# Revit family: Accessory-Towel_Arm-KOHLER-AVID-K-97498T
name_source: partatom
category: Specialty Equipment
revit_build: Autodesk Revit 2017 (Build: 20160225_1515(x64)
units: mm (PartAtom-declared; Revit-internal decimal feet)

## family parameters
Cut with Voids When Loaded = No
Host = Face
OmniClass Number = 23.31.25.25
OmniClass Title = Towel Bars
Part Type = Normal
Room Calculation Point = No
Round Connector Dimension = Use Diameter
Shared = No

## types (10) — shared parameters
ADA Compliant = No
Assembly Code = C1030200
Date Modified = 06/09/2020
Default Elevation = 42"
Description = Towel Arm
Height = 1 3/4"
Length = 2 3/4"
Manufacturer = KOHLER Co.
Master Format 2014 = 10 28 00
Master Format 2014 Name = Toilet, Bath, and Laundry Accessories
Material = Premium Metal Construction
Product Documentation Link = http://files.kohler.com.cn
Product Name = AVID
Product Page URL = http://www.kohler.com.cn
URL = http://www.kohler.com.cn
WaterSense Certified = No
Width = 9 15/16"

## per-type parameters (varying)
| type | Finish | Model | Type |
| CP-Polished Chrome | Kohler-Metal-CP-Polished_Chrome | K-97498T-CP | 1 |
| AF-Flange Gold | Kohler-Metal-AF-Flange_Gold | K-97498T-AF | 2 |
| BN-Roman Silver | Kohler-Metal-BN-Roman_Silver | K-97498T-BN | 3 |
| BV-Roman Copper | Kohler-Metal-BV-Roman_Copper | K-97498T-BV | 4 |
| PGD-Eternal Gold | Kohler-Metal-PGD-Eternal_Gold | K-97498T-PGD | 5 |
| RGD-Rose Gold | Kohler-Metal-RGD-Rose_Gold | K-97498T-RGD | 6 |
| SN-Champagne Gold | Kohler-Metal-SN-Champagne_Gold | K-97498T-SN | 7 |
| TT-Titanium Silver | Kohler-Metal-TT-Titanium_Silver | K-97498T-TT | 8 |
| 2BL-Original Black | Kohler-Metal-2BL-Original_Black | K-97498T-2BL | 9 |
| 2BZ-Elegant Black | Kohler-Metal-2BZ-Elegant_Black | K-97498T-2BZ | 10 |

## geometry (parser evidence)
native form markers: Sweep x5
no freeform markers — native parametric forms only
